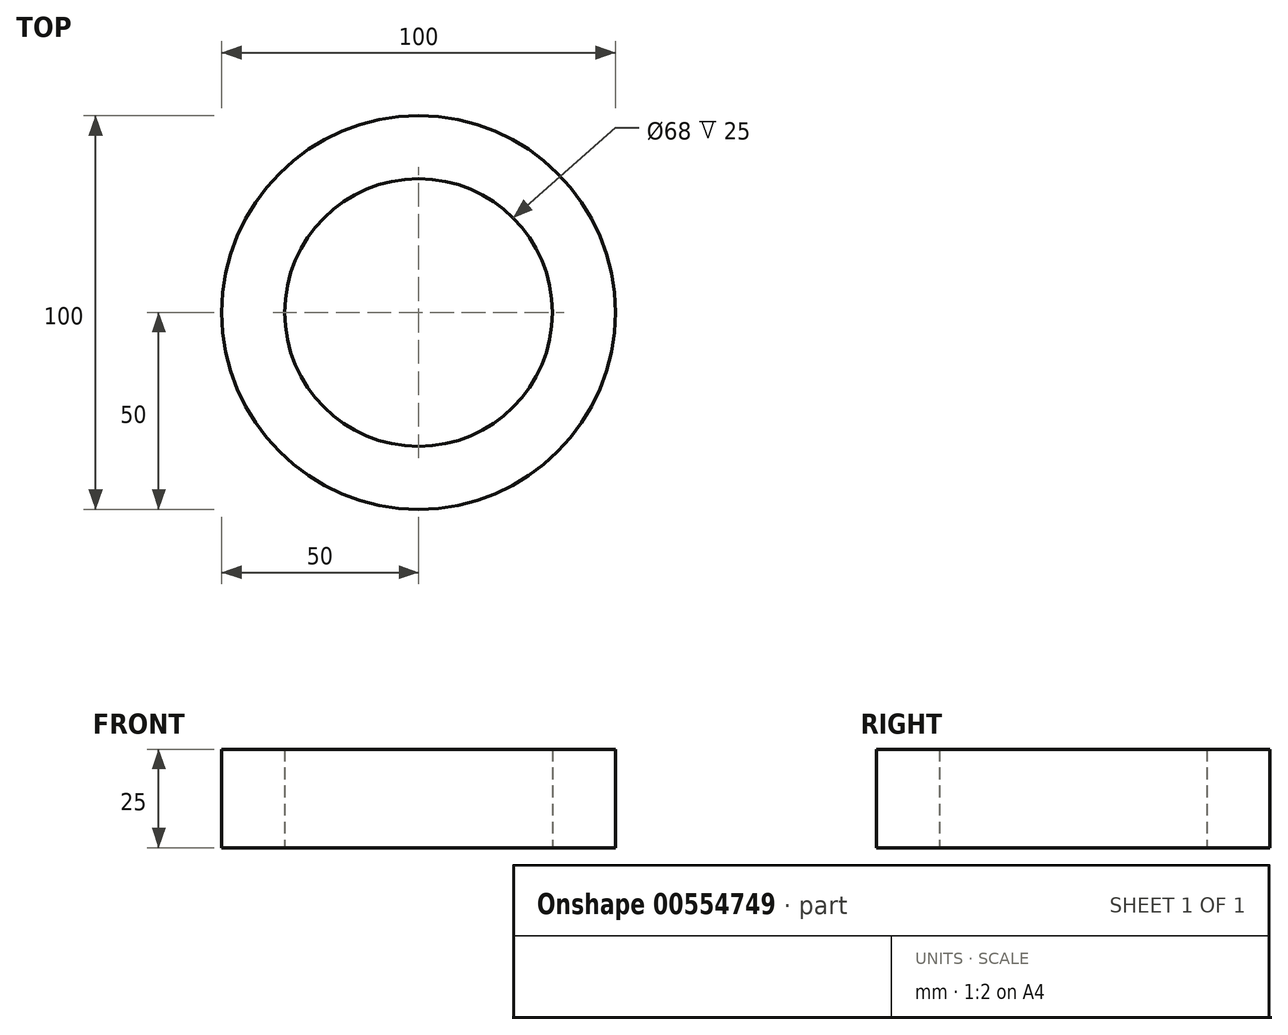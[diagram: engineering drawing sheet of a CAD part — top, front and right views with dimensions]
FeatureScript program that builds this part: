
annotation { "Feature Type Name" : "Feature", "Feature Type Description" : "" }
export const myFeature = defineFeature(function(context is Context, id is Id, definition is map)
    precondition{}
    {
        {
            var Q0;
            Q0=qCreatedBy(makeId("Top.planeOp"),FACE);
            var sketch = newSketch(context, id + "F0", { "sketchPlane" : qUnion([Q0])});
            skCircle(sketch, "E0", {"center": v(0, 0) * mm, "radius": 50 * mm});
            skCircle(sketch, "E1", {"center": v(0, 0) * mm, "radius": 34 * mm});
            skSolve(sketch);
        }
        {
            var Q0;
            Q0=makeQuery(id+"F0.imprint","IMPRINT",FACE,{"disambiguationData":[TD([[makeQuery(id+"F0.imprint","IMPRINT",EDGE,{"derivedFrom":sQuery(id+"F0.wireOp",EDGE,"E0")}),1.0]])]});
            extrude(context, id + "F1", {"entities" : qUnion([Q0]), "depth" : 25 * mm, "offsetDistance" : 25 * mm});
        }
    });
